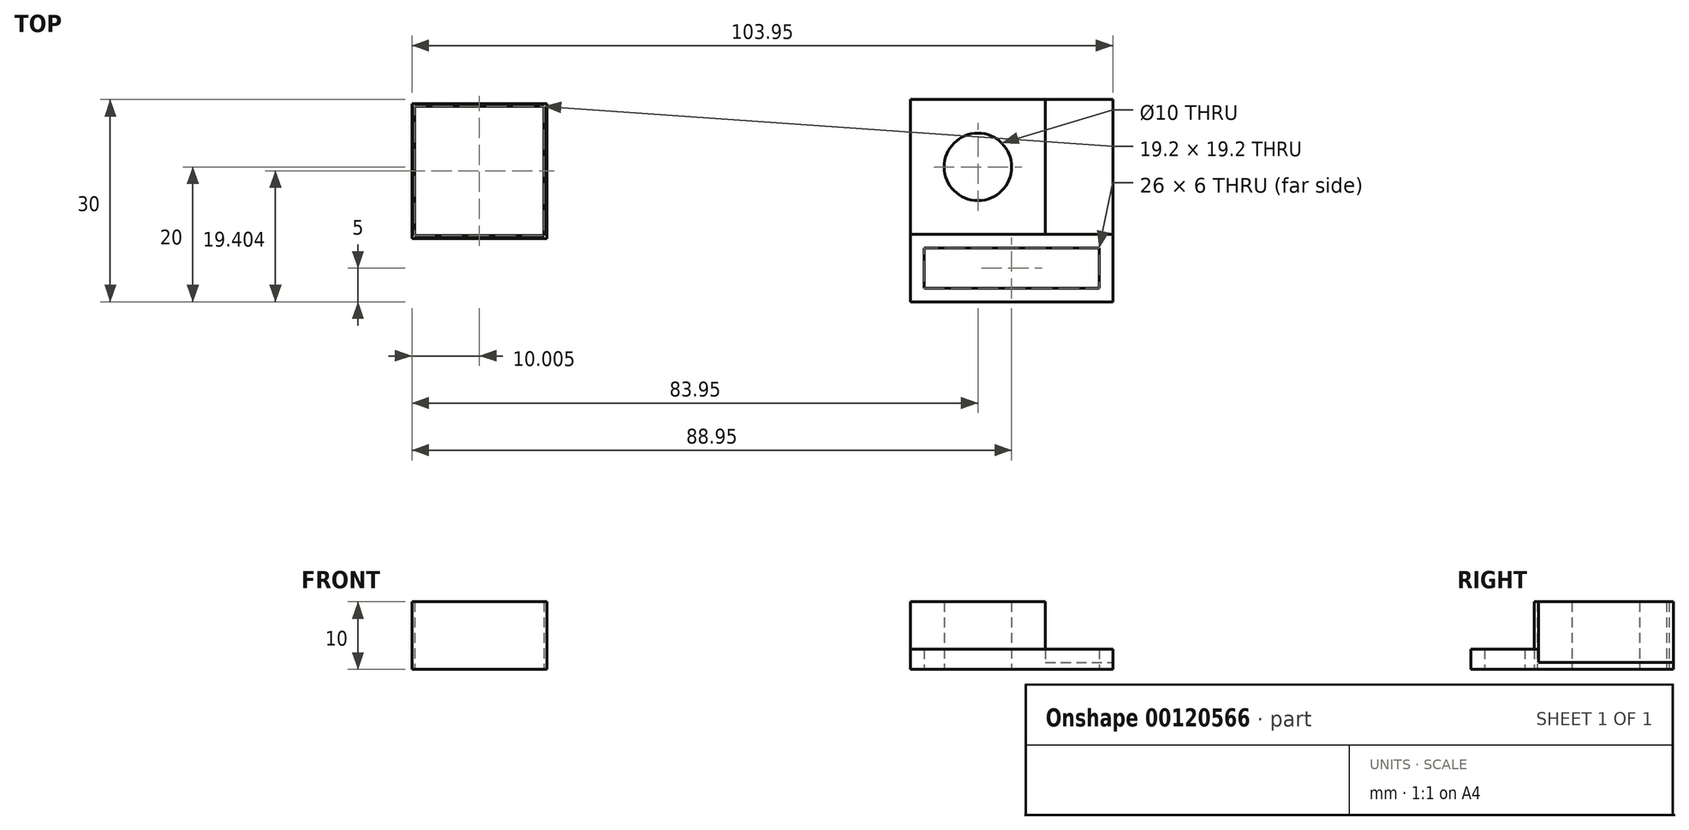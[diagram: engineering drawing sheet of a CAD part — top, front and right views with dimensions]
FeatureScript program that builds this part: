
annotation { "Feature Type Name" : "Feature", "Feature Type Description" : "" }
export const myFeature = defineFeature(function(context is Context, id is Id, definition is map)
    precondition{}
    {
        {
            var Q0;
            Q0=qCreatedBy(makeId("Top.planeOp"),FACE);
            var sketch = newSketch(context, id + "F0", { "sketchPlane" : qUnion([Q0])});
            skLineSegment(sketch, "E0.bottom", {"start": v(10, -10) * mm, "end": v(-10, -10) * mm});
            skLineSegment(sketch, "E0.top", {"start": v(10, 10) * mm, "end": v(-10, 10) * mm});
            skLineSegment(sketch, "E0.left", {"start": v(10, -10) * mm, "end": v(10, 10) * mm});
            skLineSegment(sketch, "E0.right", {"start": v(-10, -10) * mm, "end": v(-10, 10) * mm});
            skPoint(sketch, "E0.middle", {"position": v(0, 0) * mm});
            skLineSegment(sketch, "E1", {"start": v(10, 10) * mm, "end": v(20, 10) * mm});
            skLineSegment(sketch, "E2", {"start": v(20, 10) * mm, "end": v(20, -10) * mm});
            skLineSegment(sketch, "E3", {"start": v(20, -10) * mm, "end": v(10, -10) * mm});
            skCircle(sketch, "E4", {"center": v(0, 0) * mm, "radius": 5 * mm});
            skLineSegment(sketch, "E5", {"start": v(-10, -10) * mm, "end": v(-10, -20) * mm});
            skLineSegment(sketch, "E6", {"start": v(-10, -20) * mm, "end": v(20, -20) * mm});
            skLineSegment(sketch, "E7", {"start": v(20, -20) * mm, "end": v(20, -10) * mm});
            skLineSegment(sketch, "E8.0", {"start": v(-8, -18) * mm, "end": v(18, -18) * mm});
            skLineSegment(sketch, "E8.1", {"start": v(-8, -12) * mm, "end": v(-8, -18) * mm});
            skLineSegment(sketch, "E8.2", {"start": v(18, -18) * mm, "end": v(18, -12) * mm});
            skLineSegment(sketch, "E8.3", {"start": v(18, -12) * mm, "end": v(10, -12) * mm});
            skLineSegment(sketch, "E8.4", {"start": v(10, -12) * mm, "end": v(-8, -12) * mm});
            skLineSegment(sketch, "E9.bottom", {"start": v(-63.95, -10.6) * mm, "end": v(-83.95, -10.6) * mm});
            skLineSegment(sketch, "E9.top", {"start": v(-63.95, 9.4) * mm, "end": v(-83.95, 9.4) * mm});
            skLineSegment(sketch, "E9.left", {"start": v(-63.95, -10.6) * mm, "end": v(-63.95, 9.4) * mm});
            skLineSegment(sketch, "E9.right", {"start": v(-83.95, -10.6) * mm, "end": v(-83.95, 9.4) * mm});
            skPoint(sketch, "E9.middle", {"position": v(-73.95, -0.6) * mm});
            skLineSegment(sketch, "E10.0", {"start": v(-64.35, 9) * mm, "end": v(-83.55, 9) * mm});
            skLineSegment(sketch, "E10.1", {"start": v(-64.35, -10.2) * mm, "end": v(-64.35, 9) * mm});
            skLineSegment(sketch, "E10.2", {"start": v(-64.35, -10.2) * mm, "end": v(-83.55, -10.2) * mm});
            skLineSegment(sketch, "E10.3", {"start": v(-83.55, -10.2) * mm, "end": v(-83.55, 9) * mm});
            skSolve(sketch);
        }
        {
            var Q0;
            Q0=makeQuery(id+"F0.imprint","IMPRINT",FACE,{"disambiguationData":[TD([[makeQuery(id+"F0.imprint","IMPRINT",EDGE,{"derivedFrom":sQuery(id+"F0.wireOp",EDGE,"E0.bottom")}),-1.0]])]});
            extrude(context, id + "F1", {"entities" : qUnion([Q0]), "depth" : 10 * mm});
        }
        {
            var Q0;
            Q0=makeQuery(id+"F0.imprint","IMPRINT",FACE,{"disambiguationData":[TD([[makeQuery(id+"F0.imprint","IMPRINT",EDGE,{"derivedFrom":sQuery(id+"F0.wireOp",EDGE,"E0.left")}),-1.0]])]});
            extrude(context, id + "F2", {"entities" : qUnion([Q0]), "operationType" : NewBodyOperationType.ADD, "depth" : 1 * mm});
        }
        {
            var Q0;
            Q0=makeQuery(id+"F0.imprint","IMPRINT",FACE,{"disambiguationData":[TD([[makeQuery(id+"F0.imprint","IMPRINT",EDGE,{"derivedFrom":sQuery(id+"F0.wireOp",EDGE,"E0.bottom")}),1.0]])]});
            extrude(context, id + "F3", {"entities" : qUnion([Q0]), "operationType" : NewBodyOperationType.ADD, "depth" : 3 * mm});
        }
        {
            var Q0;
            Q0=makeQuery(id+"F0.imprint","IMPRINT",FACE,{"disambiguationData":[TD([[makeQuery(id+"F0.imprint","IMPRINT",EDGE,{"derivedFrom":sQuery(id+"F0.wireOp",EDGE,"E9.bottom")}),-1.0]])]});
            extrude(context, id + "F4", {"entities" : qUnion([Q0]), "depth" : 10 * mm, "offsetDistance" : 25 * mm});
        }
    });
